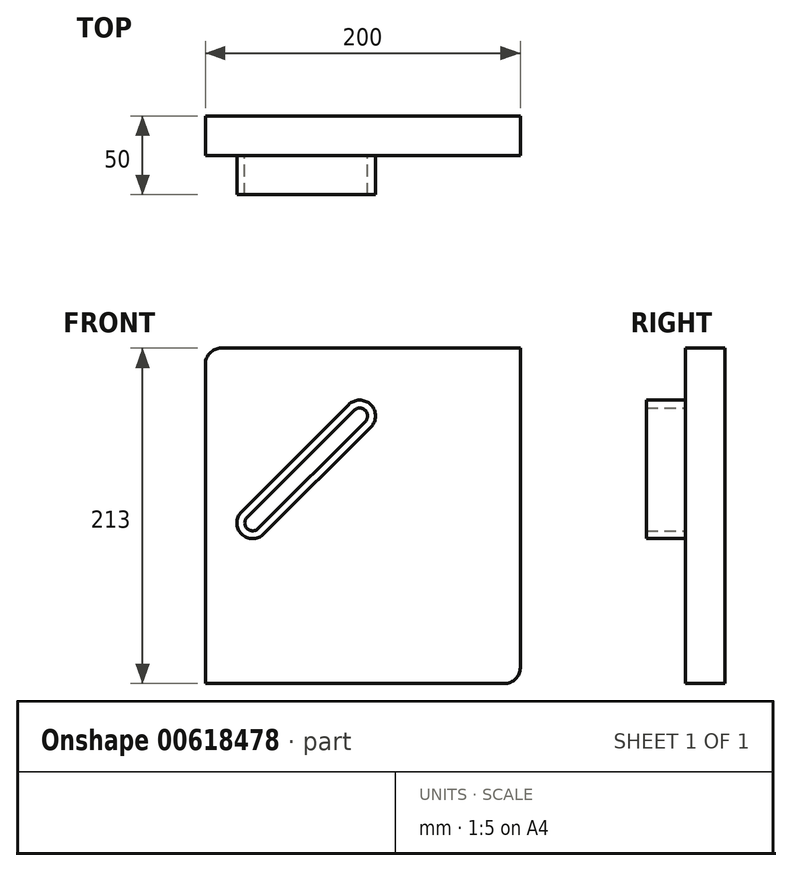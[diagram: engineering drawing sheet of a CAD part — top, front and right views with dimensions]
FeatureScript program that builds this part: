
annotation { "Feature Type Name" : "Feature", "Feature Type Description" : "" }
export const myFeature = defineFeature(function(context is Context, id is Id, definition is map)
    precondition{}
    {
        {
            var Q0;
            Q0=qCreatedBy(makeId("Front.planeOp"),FACE);
            var sketch = newSketch(context, id + "F0", { "sketchPlane" : qUnion([Q0])});
            skLineSegment(sketch, "E0.bottom", {"start": v(100, 106.5) * mm, "end": v(-90, 106.5) * mm});
            skLineSegment(sketch, "E0.top", {"start": v(90, -106.5) * mm, "end": v(-100, -106.5) * mm});
            skLineSegment(sketch, "E0.left", {"start": v(100, 106.5) * mm, "end": v(100, -96.5) * mm});
            skLineSegment(sketch, "E0.right", {"start": v(-100, 96.5) * mm, "end": v(-100, -106.5) * mm});
            skPoint(sketch, "E0.middle", {"position": v(0, 0) * mm});
            skPoint(sketch, "E1.visualSharp", {"position": v(-100, 106.5) * mm});
            skArc(sketch, "E1.filletArc", {"start": v(-90, 106.5) * mm, "mid": v(-97.07, 103.57) * mm, "end": v(-100, 96.5) * mm});
            skPoint(sketch, "E2.visualSharp", {"position": v(100, -106.5) * mm});
            skArc(sketch, "E2.filletArc", {"start": v(90, -106.5) * mm, "mid": v(97.07, -103.57) * mm, "end": v(100, -96.5) * mm});
            skSolve(sketch);
        }
        {
            var Q0;
            Q0=makeQuery(id+"F0.imprint","IMPRINT",FACE,{"disambiguationData":[TD([[makeQuery(id+"F0.imprint","IMPRINT",EDGE,{"derivedFrom":sQuery(id+"F0.wireOp",EDGE,"E0.bottom")}),1.0]])]});
            extrude(context, id + "F1", {"entities" : qUnion([Q0]), "depth" : 25 * mm, "offsetDistance" : 25.4 * mm});
        }
        {
            var Q0;
            Q0=makeQuery(id+"F1.opExtrude","CAP_FACE",FACE,{"disambiguationData":[OSD([sQuery(id+"F0.wireOp",EDGE,"E0.bottom"),sQuery(id+"F0.wireOp",EDGE,"E0.top"),sQuery(id+"F0.wireOp",EDGE,"E0.left"),sQuery(id+"F0.wireOp",EDGE,"E0.right"),sQuery(id+"F0.wireOp",EDGE,"E1.filletArc"),sQuery(id+"F0.wireOp",EDGE,"E2.filletArc")])],"isStart":false});
            var sketch = newSketch(context, id + "F2", { "sketchPlane" : qUnion([Q0])});
            skArc(sketch, "E3", {"start": v(-73.54, -0.96) * mm, "mid": v(-73.54, -8.04) * mm, "end": v(-66.46, -8.04) * mm});
            skArc(sketch, "E4", {"start": v(1.54, 59.96) * mm, "mid": v(1.54, 67.04) * mm, "end": v(-5.54, 67.04) * mm});
            skArc(sketch, "E5", {"start": v(5.07, 56.43) * mm, "mid": v(5.07, 70.57) * mm, "end": v(-9.07, 70.57) * mm});
            skArc(sketch, "E6", {"start": v(-77.07, 2.57) * mm, "mid": v(-77.07, -11.57) * mm, "end": v(-62.93, -11.57) * mm});
            skLineSegment(sketch, "E7", {"start": v(-62.93, -11.57) * mm, "end": v(5.07, 56.43) * mm});
            skLineSegment(sketch, "E8", {"start": v(-77.07, 2.57) * mm, "end": v(-9.07, 70.57) * mm});
            skLineSegment(sketch, "E9", {"start": v(-73.54, -0.96) * mm, "end": v(-5.54, 67.04) * mm});
            skLineSegment(sketch, "E10", {"start": v(-66.46, -8.04) * mm, "end": v(1.54, 59.96) * mm});
            skSolve(sketch);
        }
        {
            var Q0;
            Q0 = qSketchRegion(id + "F2", true);
            extrude(context, id + "F3", {"entities" : qUnion([Q0]), "operationType" : NewBodyOperationType.ADD, "depth" : 25 * mm, "offsetDistance" : 25.4 * mm});
        }
    });
